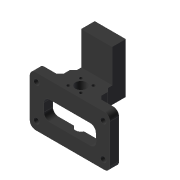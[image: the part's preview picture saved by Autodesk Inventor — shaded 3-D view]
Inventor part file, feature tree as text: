
AUTODESK INVENTOR PART (.ipt)
format: ipt  version: 2020 (Build 240168000, 168)  size: 172,544 bytes
history: native  units: mm
features: extrude x2, sketch x2, chamfer x1
ambient origin geometry x8: Origin, YZ Plane, XZ Plane, XY Plane, X Axis, Y Axis, Z Axis, Center Point
bodies: Solid1 (feature_tree)
feature tree (5):
  extrude  "Extrusion1"  Depth=27.641794mm
  extrude  "Extrusion2"  Depth=12.0mm
  sketch  "Sketch1"  dims[d0=16.0mm d1=27.641794mm]
  sketch  "Sketch2"  dims[d2=14.75mm d3=0.0mm d4=12.0mm d5=30.0mm d6=0.0mm]
  chamfer  "Chamfer3"  Distance=30.0mm
